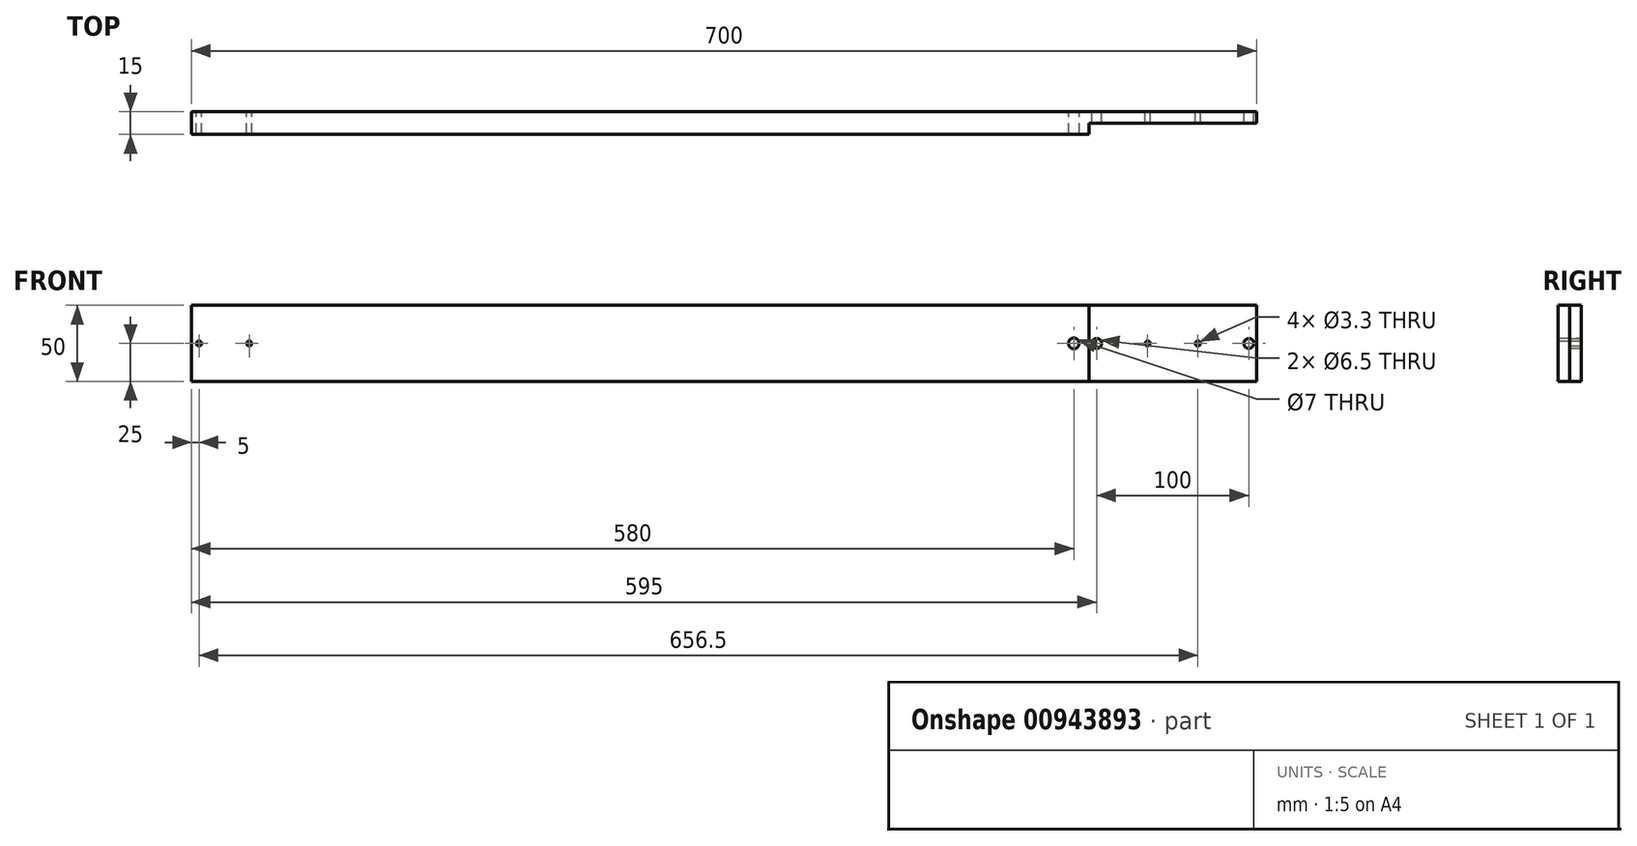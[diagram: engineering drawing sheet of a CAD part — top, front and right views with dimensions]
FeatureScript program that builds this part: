
annotation { "Feature Type Name" : "Feature", "Feature Type Description" : "" }
export const myFeature = defineFeature(function(context is Context, id is Id, definition is map)
    precondition{}
    {
        {
            var Q0;
            Q0=qCreatedBy(makeId("Front.planeOp"),FACE);
            var sketch = newSketch(context, id + "F0", { "sketchPlane" : qUnion([Q0])});
            skLineSegment(sketch, "E0.bottom", {"start": v(-350, 25) * mm, "end": v(350, 25) * mm});
            skLineSegment(sketch, "E0.top", {"start": v(-350, -25) * mm, "end": v(350, -25) * mm});
            skLineSegment(sketch, "E0.left", {"start": v(-350, 25) * mm, "end": v(-350, -25) * mm});
            skLineSegment(sketch, "E0.right", {"start": v(350, 25) * mm, "end": v(350, -25) * mm});
            skPoint(sketch, "E0.middle", {"position": v(0, 0) * mm});
            skSolve(sketch);
        }
        {
            var Q0;
            Q0 = qSketchRegion(id + "F0", true);
            extrude(context, id + "F1", {"entities" : qUnion([Q0]), "depth" : 15 * mm, "offsetDistance" : 25 * mm});
        }
        {
            var Q0;
            Q0=makeQuery(id+"F1.opExtrude","SWEPT_FACE",FACE,{"disambiguationData":[OSD([sQuery(id+"F0.wireOp",EDGE,"E0.top")])]});
            var sketch = newSketch(context, id + "F2", { "sketchPlane" : qUnion([Q0])});
            skLineSegment(sketch, "E1", {"start": v(350, 15) * mm, "end": v(350, 7.5) * mm});
            skLineSegment(sketch, "E2", {"start": v(350, 7.5) * mm, "end": v(240, 7.5) * mm});
            skLineSegment(sketch, "E3", {"start": v(240, 7.5) * mm, "end": v(240, 15) * mm});
            skLineSegment(sketch, "E4", {"start": v(240, 15) * mm, "end": v(350, 15) * mm});
            skSolve(sketch);
        }
        {
            var Q0;
            Q0 = qSketchRegion(id + "F2", true);
            extrude(context, id + "F3", {"entities" : qUnion([Q0]), "operationType" : NewBodyOperationType.REMOVE, "endBound" : BoundingType.THROUGH_ALL, "oppositeDirection" : true, "depth" : 25 * mm, "offsetDistance" : 25 * mm});
        }
        {
            var Q0;
            Q0=makeQuery(id+"F1.opExtrude","CAP_FACE",FACE,{"disambiguationData":[OSD([sQuery(id+"F0.wireOp",EDGE,"E0.bottom"),sQuery(id+"F0.wireOp",EDGE,"E0.top"),sQuery(id+"F0.wireOp",EDGE,"E0.left"),sQuery(id+"F0.wireOp",EDGE,"E0.right")])],"isStart":true});
            var sketch = newSketch(context, id + "F4", { "sketchPlane" : qUnion([Q0])});
            skPoint(sketch, "E5", {"position": v(-311.5, 0) * mm});
            skPoint(sketch, "E6", {"position": v(-278.5, 0) * mm});
            skLineSegment(sketch, "E7", {"start": v(-295, 25) * mm, "end": v(-295, -25) * mm, "construction": true});
            skSolve(sketch);
        }
        {
            var Q0;
            Q0=sQuery(id+"F4.wireOp",VERTEX,"E5");
            var Q1;
            Q1=sQuery(id+"F4.wireOp",VERTEX,"E6");
            var Q2;
            Q2=makeQuery(id+"F1.opExtrude","SWEPT_BODY",BODY,{"disambiguationData":[OSD([sQuery(id+"F0.wireOp",EDGE,"E0.bottom"),sQuery(id+"F0.wireOp",EDGE,"E0.top"),sQuery(id+"F0.wireOp",EDGE,"E0.left"),sQuery(id+"F0.wireOp",EDGE,"E0.right")])]});
            hole(context, id + "F5", {"style" : HoleStyle.SIMPLE, "endStyle" : HoleEndStyle.THROUGH, "standardTappedOrClearance" : lookupTablePath({ "standard" : "ISO", "engagement" : "75%", "pitch" : "0.7 mm", "size" : "M4", "type" : "Tapped" }), "standardBlindInLast" : lookupTablePath({ "standard" : "ISO", "fit" : "Normal", "engagement" : "75%", "pitch" : "0.7 mm", "size" : "M4", "type" : "Clearance & tapped" }), "holeDiameter" : 3.3 * mm, "majorDiameter" : 4 * mm, "showTappedDepth" : true, "isTappedThrough" : true, "tappedDepth" : 20 * mm, "tapClearance" : 3, "locations" : qUnion([Q0, Q1]), "scope" : qUnion([Q2])});
        }
        {
            var Q0;
            Q0=makeQuery(id+"F1.opExtrude","CAP_FACE",FACE,{"disambiguationData":[OSD([sQuery(id+"F0.wireOp",EDGE,"E0.bottom"),sQuery(id+"F0.wireOp",EDGE,"E0.top"),sQuery(id+"F0.wireOp",EDGE,"E0.left"),sQuery(id+"F0.wireOp",EDGE,"E0.right")])],"isStart":true});
            var sketch = newSketch(context, id + "F6", { "sketchPlane" : qUnion([Q0])});
            skPoint(sketch, "E8", {"position": v(345, 0) * mm});
            skPoint(sketch, "E9", {"position": v(312, 0) * mm});
            skSolve(sketch);
        }
        {
            var Q0;
            Q0=sQuery(id+"F6.wireOp",VERTEX,"E9");
            var Q1;
            Q1=sQuery(id+"F6.wireOp",VERTEX,"E8");
            var Q2;
            Q2=makeQuery(id+"F1.opExtrude","SWEPT_BODY",BODY,{"disambiguationData":[OSD([sQuery(id+"F0.wireOp",EDGE,"E0.bottom"),sQuery(id+"F0.wireOp",EDGE,"E0.top"),sQuery(id+"F0.wireOp",EDGE,"E0.left"),sQuery(id+"F0.wireOp",EDGE,"E0.right")])]});
            hole(context, id + "F7", {"style" : HoleStyle.SIMPLE, "endStyle" : HoleEndStyle.THROUGH, "standardTappedOrClearance" : lookupTablePath({ "standard" : "ISO", "engagement" : "75%", "pitch" : "0.7 mm", "size" : "M4", "type" : "Tapped" }), "standardBlindInLast" : lookupTablePath({ "standard" : "ISO", "fit" : "Normal", "engagement" : "75%", "pitch" : "0.7 mm", "size" : "M4", "type" : "Clearance & tapped" }), "holeDiameter" : 3.3 * mm, "majorDiameter" : 4 * mm, "showTappedDepth" : true, "isTappedThrough" : true, "tappedDepth" : 20 * mm, "tapClearance" : 3, "locations" : qUnion([Q0, Q1]), "scope" : qUnion([Q2])});
        }
        {
            var Q0;
            Q0=makeQuery(id+"F1.opExtrude","CAP_FACE",FACE,{"disambiguationData":[OSD([sQuery(id+"F0.wireOp",EDGE,"E0.bottom"),sQuery(id+"F0.wireOp",EDGE,"E0.top"),sQuery(id+"F0.wireOp",EDGE,"E0.left"),sQuery(id+"F0.wireOp",EDGE,"E0.right")])],"isStart":true});
            var sketch = newSketch(context, id + "F8", { "sketchPlane" : qUnion([Q0])});
            skLineSegment(sketch, "E10", {"start": v(-300, -25) * mm, "end": v(-300, 25) * mm, "construction": true});
            skPoint(sketch, "E11", {"position": v(-230, 0) * mm});
            skSolve(sketch);
        }
        {
            var Q0;
            Q0=sQuery(id+"F8.wireOp",VERTEX,"E11");
            var Q1;
            Q1=makeQuery(id+"F1.opExtrude","SWEPT_BODY",BODY,{"disambiguationData":[OSD([sQuery(id+"F0.wireOp",EDGE,"E0.bottom"),sQuery(id+"F0.wireOp",EDGE,"E0.top"),sQuery(id+"F0.wireOp",EDGE,"E0.left"),sQuery(id+"F0.wireOp",EDGE,"E0.right")])]});
            hole(context, id + "F9", {"style" : HoleStyle.SIMPLE, "endStyle" : HoleEndStyle.THROUGH, "standardTappedOrClearance" : lookupTablePath({ "standard" : "ISO", "size" : "7", "type" : "Drilled" }), "standardBlindInLast" : lookupTablePath({ "standard" : "ISO", "size" : "7", "type" : "Drilled" }), "holeDiameter" : 7 * mm, "majorDiameter" : 6 * mm, "tappedDepth" : 20 * mm, "tapClearance" : 3, "startFromSketch" : true, "locations" : qUnion([Q0]), "scope" : qUnion([Q1])});
        }
        {
            var Q0;
            Q0=makeQuery(id+"F1.opExtrude","CAP_FACE",FACE,{"disambiguationData":[OSD([sQuery(id+"F0.wireOp",EDGE,"E0.bottom"),sQuery(id+"F0.wireOp",EDGE,"E0.top"),sQuery(id+"F0.wireOp",EDGE,"E0.left"),sQuery(id+"F0.wireOp",EDGE,"E0.right")])],"isStart":true});
            var sketch = newSketch(context, id + "F10", { "sketchPlane" : qUnion([Q0])});
            skPoint(sketch, "E12", {"position": v(-345, 0) * mm});
            skPoint(sketch, "E13", {"position": v(-245, 0) * mm});
            skLineSegment(sketch, "E14", {"start": v(-295, 25) * mm, "end": v(-295, -25) * mm, "construction": true});
            skSolve(sketch);
        }
        {
            var Q0;
            Q0=sQuery(id+"F10.wireOp",VERTEX,"E12");
            var Q1;
            Q1=sQuery(id+"F10.wireOp",VERTEX,"E13");
            var Q2;
            Q2=makeQuery(id+"F1.opExtrude","SWEPT_BODY",BODY,{"disambiguationData":[OSD([sQuery(id+"F0.wireOp",EDGE,"E0.bottom"),sQuery(id+"F0.wireOp",EDGE,"E0.top"),sQuery(id+"F0.wireOp",EDGE,"E0.left"),sQuery(id+"F0.wireOp",EDGE,"E0.right")])]});
            hole(context, id + "F11", {"style" : HoleStyle.SIMPLE, "endStyle" : HoleEndStyle.THROUGH, "standardTappedOrClearance" : lookupTablePath({ "standard" : "ISO", "size" : "6.5", "type" : "Drilled" }), "standardBlindInLast" : lookupTablePath({ "standard" : "ISO", "size" : "6.5", "type" : "Drilled" }), "holeDiameter" : 6.5 * mm, "majorDiameter" : 5 * mm, "tappedDepth" : 20 * mm, "tapClearance" : 3, "locations" : qUnion([Q0, Q1]), "scope" : qUnion([Q2])});
        }
    });
